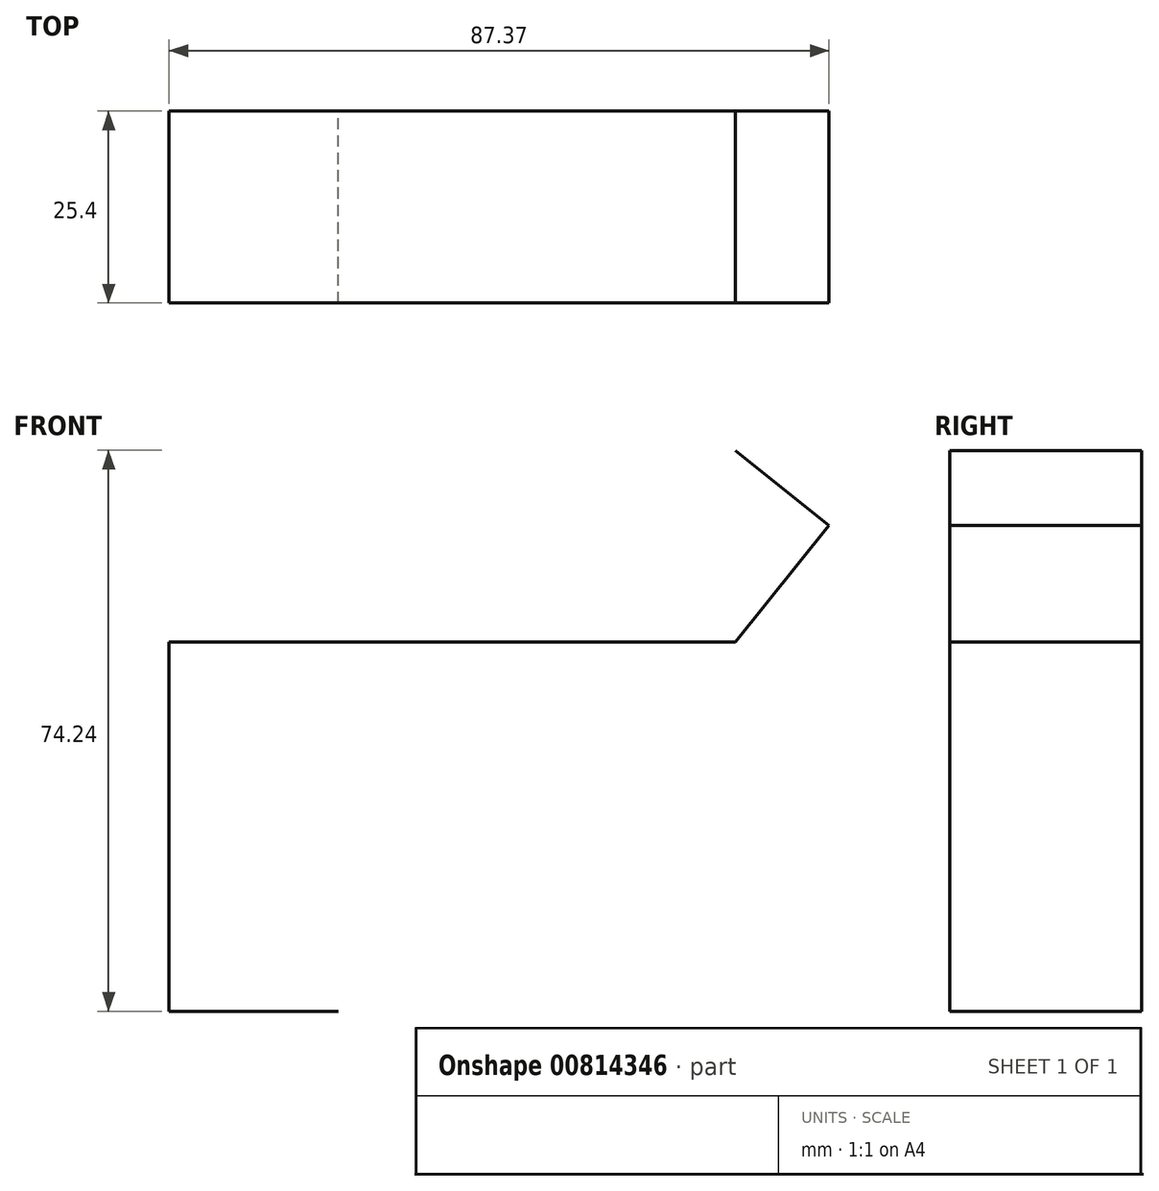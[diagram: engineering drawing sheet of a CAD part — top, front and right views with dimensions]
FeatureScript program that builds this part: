
annotation { "Feature Type Name" : "Feature", "Feature Type Description" : "" }
export const myFeature = defineFeature(function(context is Context, id is Id, definition is map)
    precondition{}
    {
        {
            var Q0;
            Q0=qCreatedBy(makeId("Front.planeOp"),FACE);
            var sketch = newSketch(context, id + "F0", { "sketchPlane" : qUnion([Q0])});
            skLineSegment(sketch, "E0", {"start": v(-40.67, -16.57) * mm, "end": v(-63.1, -16.57) * mm});
            skLineSegment(sketch, "E1", {"start": v(-63.1, -16.57) * mm, "end": v(-63.1, 32.3) * mm});
            skLineSegment(sketch, "E2", {"start": v(-63.1, 32.3) * mm, "end": v(11.88, 32.3) * mm});
            skLineSegment(sketch, "E3", {"start": v(11.88, 32.3) * mm, "end": v(24.27, 47.7) * mm});
            skLineSegment(sketch, "E4", {"start": v(24.27, 47.7) * mm, "end": v(11.88, 57.67) * mm});
            skSolve(sketch);
        }
        {
            var Q0;
            Q0 = qSketchRegion(id + "F0", true);
            var Q1;
            Q1 = qConstructionFilter(qBodyType(qCreatedBy(id + "F0" ,EDGE), BodyType.WIRE), ConstructionObject.NO);
            extrude(context, id + "F1", {"entities" : qUnion([Q0]), "bodyType" : ToolBodyType.SURFACE, "surfaceEntities" : qUnion([Q1]), "oppositeDirection" : true, "depth" : 25.4 * mm, "offsetDistance" : 25.4 * mm});
        }
    });
